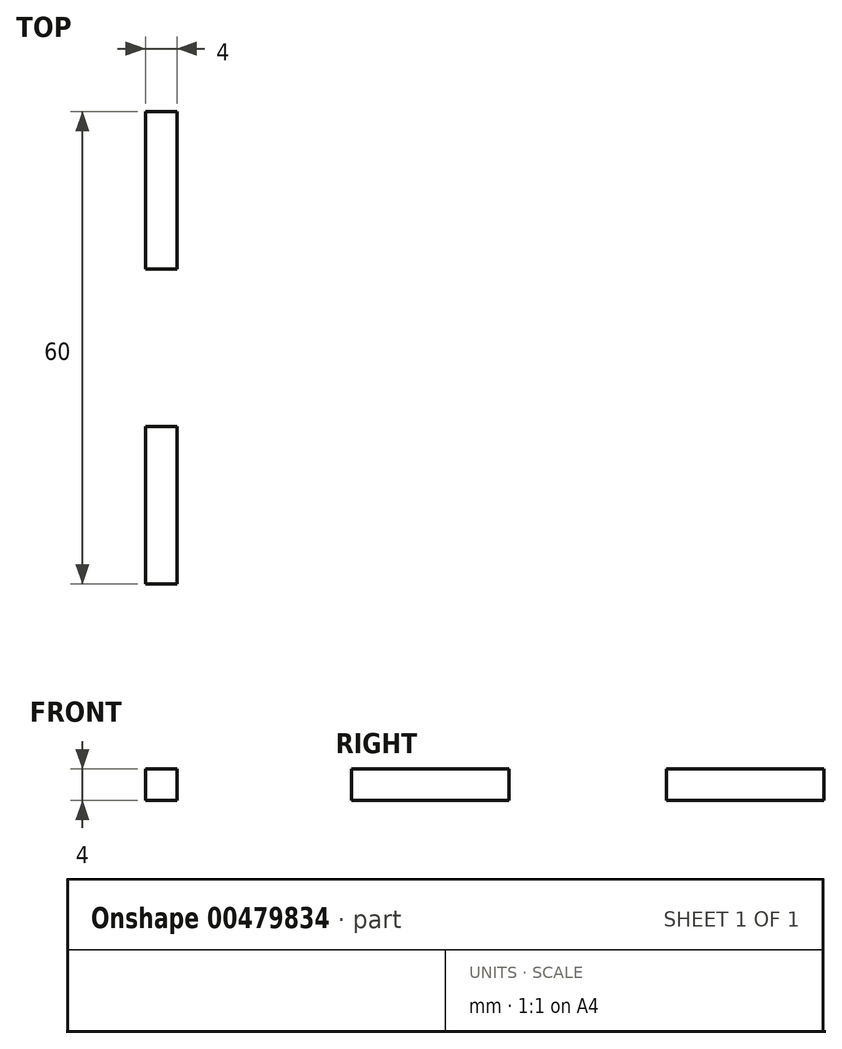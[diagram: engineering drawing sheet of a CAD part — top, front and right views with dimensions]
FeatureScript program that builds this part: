
annotation { "Feature Type Name" : "Feature", "Feature Type Description" : "" }
export const myFeature = defineFeature(function(context is Context, id is Id, definition is map)
    precondition{}
    {
        {
            var Q0;
            Q0=qCreatedBy(makeId("Right.planeOp"),FACE);
            var sketch = newSketch(context, id + "F0", { "sketchPlane" : qUnion([Q0])});
            skLineSegment(sketch, "E0.bottom", {"start": v(0, 0) * mm, "end": v(60, 0) * mm});
            skLineSegment(sketch, "E0.top", {"start": v(0, 50) * mm, "end": v(46, 50) * mm});
            skLineSegment(sketch, "E0.left", {"start": v(0, 0) * mm, "end": v(0, 50) * mm});
            skLineSegment(sketch, "E0.right", {"start": v(60, 0) * mm, "end": v(60, 50) * mm});
            skLineSegment(sketch, "E1.left", {"start": v(60, 50) * mm, "end": v(60, 54) * mm});
            skLineSegment(sketch, "E1.right", {"start": v(46, 50) * mm, "end": v(46, 54) * mm});
            skArc(sketch, "E2", {"start": v(60, 54) * mm, "mid": v(53, 61) * mm, "end": v(46, 54) * mm});
            skCircle(sketch, "E3", {"center": v(53, 54) * mm, "radius": 3 * mm});
            skLineSegment(sketch, "E4.bottom", {"start": v(0, 0) * mm, "end": v(20, 0) * mm});
            skLineSegment(sketch, "E4.top", {"start": v(0, 4) * mm, "end": v(20, 4) * mm});
            skLineSegment(sketch, "E4.left", {"start": v(0, 0) * mm, "end": v(0, 4) * mm});
            skLineSegment(sketch, "E4.right", {"start": v(20, 0) * mm, "end": v(20, 4) * mm});
            skLineSegment(sketch, "E5.bottom", {"start": v(60, 0) * mm, "end": v(40, 0) * mm});
            skLineSegment(sketch, "E5.top", {"start": v(60, 4) * mm, "end": v(40, 4) * mm});
            skLineSegment(sketch, "E5.left", {"start": v(60, 0) * mm, "end": v(60, 4) * mm});
            skLineSegment(sketch, "E5.right", {"start": v(40, 0) * mm, "end": v(40, 4) * mm});
            skLineSegment(sketch, "E6.bottom", {"start": v(0, 50) * mm, "end": v(4, 50) * mm});
            skLineSegment(sketch, "E6.top", {"start": v(0, 35) * mm, "end": v(4, 35) * mm});
            skLineSegment(sketch, "E6.left", {"start": v(0, 50) * mm, "end": v(0, 35) * mm});
            skLineSegment(sketch, "E6.right", {"start": v(4, 50) * mm, "end": v(4, 35) * mm});
            skLineSegment(sketch, "E7.bottom", {"start": v(60, 50) * mm, "end": v(56, 50) * mm});
            skLineSegment(sketch, "E7.top", {"start": v(60, 35) * mm, "end": v(56, 35) * mm});
            skLineSegment(sketch, "E7.left", {"start": v(60, 50) * mm, "end": v(60, 35) * mm});
            skLineSegment(sketch, "E7.right", {"start": v(56, 50) * mm, "end": v(56, 35) * mm});
            skLineSegment(sketch, "E8.bottom", {"start": v(60, 4) * mm, "end": v(56, 4) * mm});
            skLineSegment(sketch, "E8.top", {"start": v(60, 19) * mm, "end": v(56, 19) * mm});
            skLineSegment(sketch, "E8.left", {"start": v(60, 4) * mm, "end": v(60, 19) * mm});
            skLineSegment(sketch, "E8.right", {"start": v(56, 4) * mm, "end": v(56, 19) * mm});
            skLineSegment(sketch, "E9.bottom", {"start": v(0, 4) * mm, "end": v(4.51, 4) * mm});
            skLineSegment(sketch, "E9.top", {"start": v(0, 19) * mm, "end": v(4.51, 19) * mm});
            skLineSegment(sketch, "E9.left", {"start": v(0, 4) * mm, "end": v(0, 19) * mm});
            skLineSegment(sketch, "E9.right", {"start": v(4.51, 4) * mm, "end": v(4.51, 19) * mm});
            skSolve(sketch);
        }
        {
            var Q0;
            Q0=makeQuery(id+"F0.imprint","IMPRINT",FACE,{"disambiguationData":[TD([[makeQuery(id+"F0.imprint","IMPRINT",EDGE,{"derivedFrom":sQuery(id+"F0.wireOp",EDGE,"E0.bottom")}),1.0]])]});
            extrude(context, id + "F1", {"entities" : qUnion([Q0]), "depth" : 4 * mm});
        }
    });
